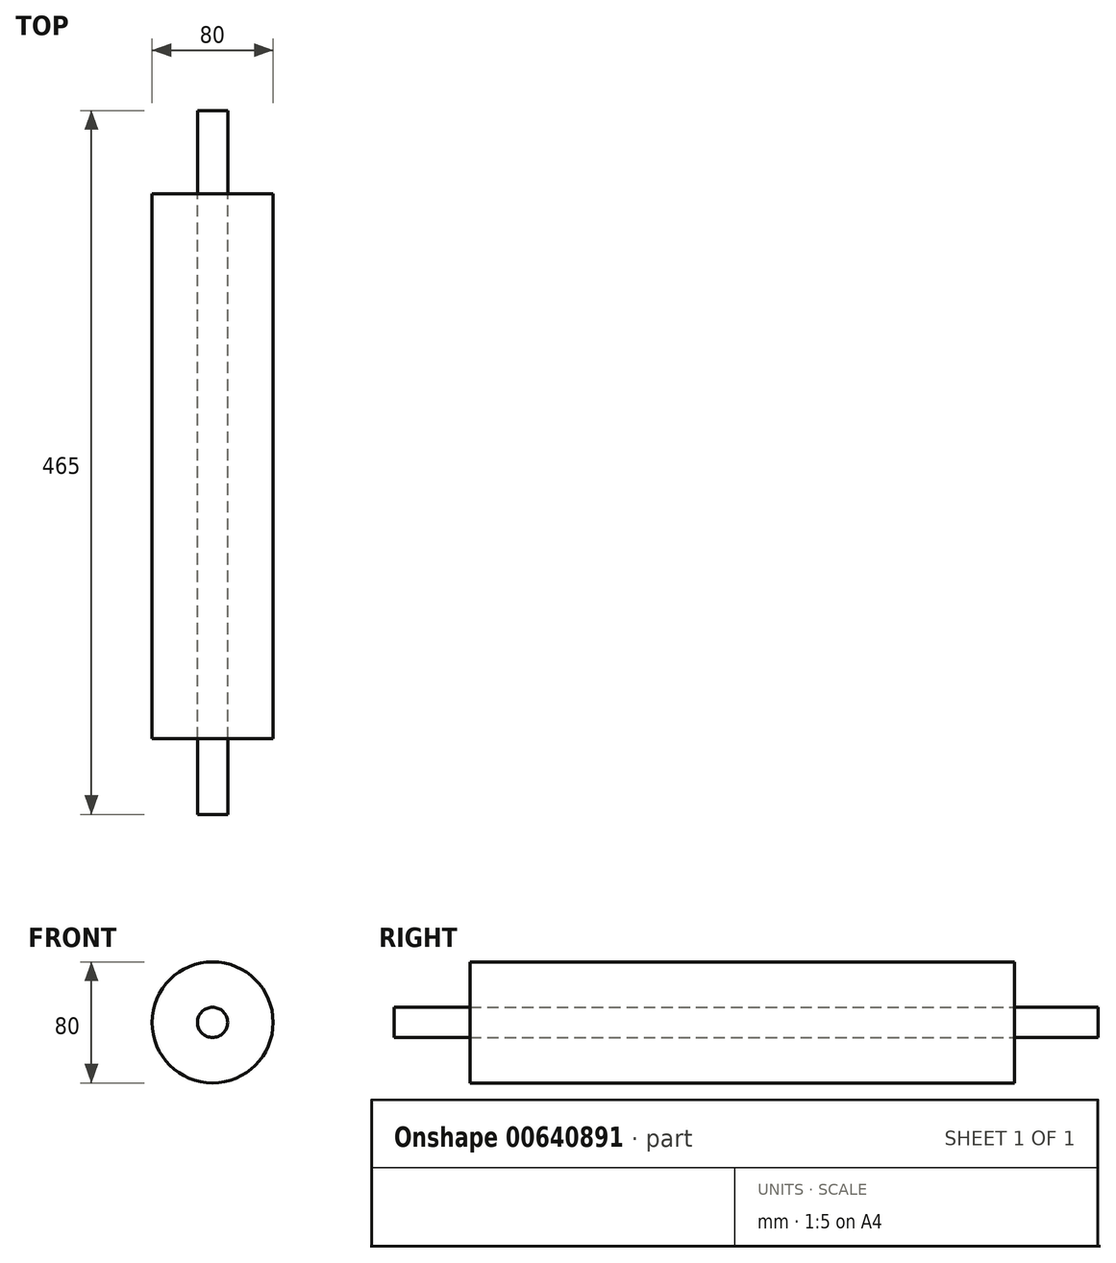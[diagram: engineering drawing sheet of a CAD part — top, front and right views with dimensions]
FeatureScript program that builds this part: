
annotation { "Feature Type Name" : "Feature", "Feature Type Description" : "" }
export const myFeature = defineFeature(function(context is Context, id is Id, definition is map)
    precondition{}
    {
        {
            var Q0;
            Q0=qCreatedBy(makeId("Front.planeOp"),FACE);
            var sketch = newSketch(context, id + "F0", { "sketchPlane" : qUnion([Q0])});
            skCircle(sketch, "E0", {"center": v(0, 0) * mm, "radius": 10 * mm});
            skSolve(sketch);
        }
        {
            var Q0;
            Q0=makeQuery(id+"F0.imprint","IMPRINT",FACE,{"disambiguationData":[TD([[makeQuery(id+"F0.imprint","IMPRINT",EDGE,{"derivedFrom":sQuery(id+"F0.wireOp",EDGE,"E0")}),1.0]])]});
            extrude(context, id + "F1", {"entities" : qUnion([Q0]), "endBound" : BoundingType.SYMMETRIC, "depth" : 465 * mm, "offsetDistance" : 25.4 * mm});
        }
        {
            var Q0;
            Q0=makeQuery(id+"F1.opExtrude","CAP_FACE",FACE,{"disambiguationData":[OSD([sQuery(id+"F0.wireOp",EDGE,"E0")])],"isStart":false});
            cPlane(context, id + "F2", {"entities" : qUnion([Q0]), "cplaneType" : CPlaneType.OFFSET, "offset" : 230 * mm, "oppositeDirection" : true, "width" : 152.4 * mm, "height" : 152.4 * mm});
        }
        {
            var Q0;
            Q0=qCreatedBy(id+"F2.planeOp",FACE);
            var sketch = newSketch(context, id + "F3", { "sketchPlane" : qUnion([Q0])});
            skCircle(sketch, "E1", {"center": v(0, 0) * mm, "radius": 40 * mm});
            skSolve(sketch);
        }
        {
            var Q0;
            Q0 = qSketchRegion(id + "F3", true);
            extrude(context, id + "F4", {"entities" : qUnion([Q0]), "endBound" : BoundingType.SYMMETRIC, "depth" : 360 * mm, "offsetDistance" : 25.4 * mm});
        }
    });
